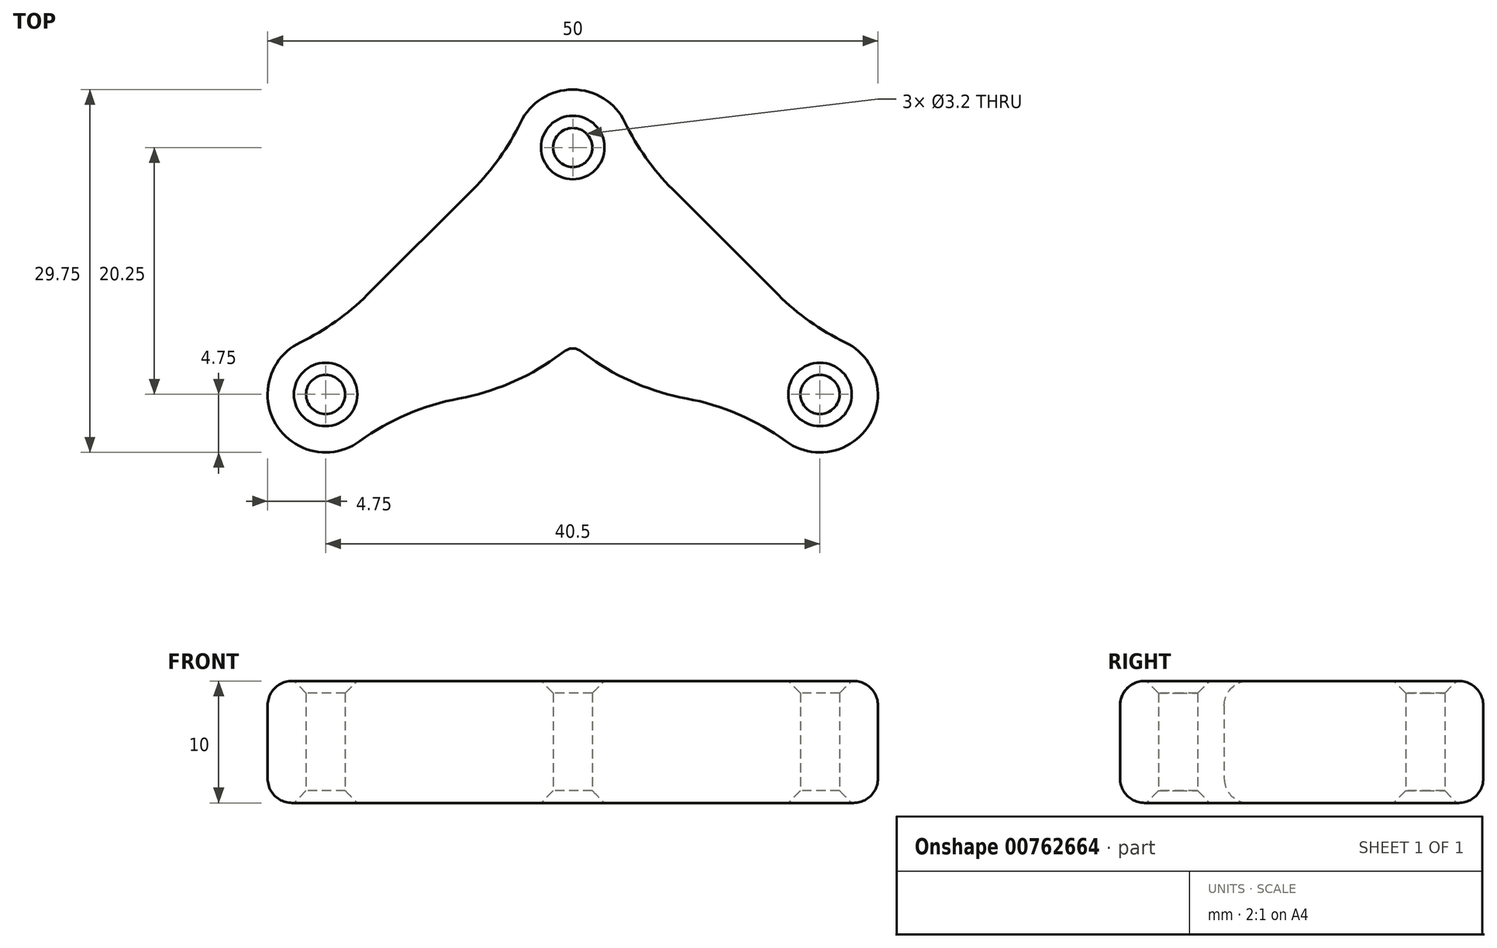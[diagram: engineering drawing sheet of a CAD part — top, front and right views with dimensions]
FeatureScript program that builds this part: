
annotation { "Feature Type Name" : "Feature", "Feature Type Description" : "" }
export const myFeature = defineFeature(function(context is Context, id is Id, definition is map)
    precondition{}
    {
        {
            var Q0;
            Q0=qCreatedBy(makeId("Top.planeOp"),FACE);
            var sketch = newSketch(context, id + "F0", { "sketchPlane" : qUnion([Q0])});
            skLineSegment(sketch, "E0", {"start": v(16.84, 8.16) * mm, "end": v(8.16, 16.84) * mm});
            skLineSegment(sketch, "E1", {"start": v(0, 3.78) * mm, "end": v(0, 4) * mm});
            skArc(sketch, "E2", {"start": v(0, 18.65) * mm, "mid": v(1.6, 20.25) * mm, "end": v(0, 21.85) * mm});
            skCircle(sketch, "E3", {"center": v(20.25, 0) * mm, "radius": 1.6 * mm});
            skArc(sketch, "E4", {"start": v(17.45, -3.84) * mm, "mid": v(24.33, -2.44) * mm, "end": v(22.3, 4.28) * mm});
            skArc(sketch, "E5", {"start": v(4.28, 22.3) * mm, "mid": v(2.53, 24.27) * mm, "end": v(0, 25) * mm});
            skPoint(sketch, "E6.visualSharp", {"position": v(4.75, 20.25) * mm});
            skArc(sketch, "E6.filletArc", {"start": v(4.28, 22.3) * mm, "mid": v(5.99, 19.41) * mm, "end": v(8.16, 16.84) * mm});
            skPoint(sketch, "E7.visualSharp", {"position": v(20.25, 4.75) * mm});
            skArc(sketch, "E7.filletArc", {"start": v(16.84, 8.16) * mm, "mid": v(19.41, 5.99) * mm, "end": v(22.3, 4.28) * mm});
            skArc(sketch, "E8.filletArc", {"start": v(17.45, -3.84) * mm, "mid": v(13.58, -1.63) * mm, "end": v(9.32, -0.34) * mm});
            skLineSegment(sketch, "E9", {"start": v(0, 4) * mm, "end": v(0, 3.78) * mm});
            skLineSegment(sketch, "E10", {"start": v(0.58, 3.6) * mm, "end": v(1.44, 2.99) * mm});
            skPoint(sketch, "E11.visualSharp", {"position": v(5.67, 0) * mm});
            skArc(sketch, "E11.filletArc", {"start": v(1.44, 2.99) * mm, "mid": v(5.2, 0.9) * mm, "end": v(9.32, -0.34) * mm});
            skArc(sketch, "E12.MirrorCS", {"start": v(-4.28, 22.3) * mm, "mid": v(-2.53, 24.27) * mm, "end": v(0, 25) * mm});
            skPoint(sketch, "E13.MirrorP", {"position": v(-4.75, 20.25) * mm});
            skArc(sketch, "E14.MirrorCS", {"start": v(-4.28, 22.3) * mm, "mid": v(-5.99, 19.41) * mm, "end": v(-8.16, 16.84) * mm});
            skLineSegment(sketch, "E15.MirrorCS", {"start": v(-16.84, 8.16) * mm, "end": v(-8.16, 16.84) * mm});
            skArc(sketch, "E16.MirrorCS", {"start": v(-16.84, 8.16) * mm, "mid": v(-19.41, 5.99) * mm, "end": v(-22.3, 4.28) * mm});
            skArc(sketch, "E17.MirrorCS", {"start": v(-17.45, -3.84) * mm, "mid": v(-24.33, -2.44) * mm, "end": v(-22.3, 4.28) * mm});
            skArc(sketch, "E18.MirrorCS", {"start": v(-17.45, -3.84) * mm, "mid": v(-13.58, -1.63) * mm, "end": v(-9.32, -0.34) * mm});
            skArc(sketch, "E19.MirrorCS", {"start": v(-1.44, 2.99) * mm, "mid": v(-5.2, 0.9) * mm, "end": v(-9.32, -0.34) * mm});
            skCircle(sketch, "E20.MirrorC", {"center": v(-20.25, 0) * mm, "radius": 1.6 * mm});
            skArc(sketch, "E21.MirrorCS", {"start": v(0, 18.65) * mm, "mid": v(-1.6, 20.25) * mm, "end": v(0, 21.85) * mm});
            skLineSegment(sketch, "E22.MirrorCS", {"start": v(-0.58, 3.6) * mm, "end": v(-1.44, 2.99) * mm});
            skPoint(sketch, "E23.visualSharp", {"position": v(0, 4) * mm});
            skArc(sketch, "E23.filletArc", {"start": v(0.58, 3.6) * mm, "mid": v(0, 3.78) * mm, "end": v(-0.58, 3.6) * mm});
            skPoint(sketch, "E24.orphan", {"position": v(0, 0) * mm});
            skSolve(sketch);
        }
        {
            var Q0;
            Q0 = qSketchRegion(id + "F0", true);
            extrude(context, id + "F1", {"entities" : qUnion([Q0]), "depth" : 10 * mm, "offsetDistance" : 25 * mm});
        }
        {
            var Q0;
            Q0=makeQuery(id+"F1.opExtrude","CAP_EDGE",EDGE,{"disambiguationData":[OSD([sQuery(id+"F0.wireOp",EDGE,"E19.MirrorCS")])],"isStart":false});
            var Q1;
            Q1=makeQuery(id+"F1.opExtrude","CAP_EDGE",EDGE,{"disambiguationData":[OSD([sQuery(id+"F0.wireOp",EDGE,"E19.MirrorCS")])],"isStart":true});
            var Q2;
            Q2=makeQuery(id+"F1.opExtrude","CAP_EDGE",EDGE,{"disambiguationData":[OSD([sQuery(id+"F0.wireOp",EDGE,"E15.MirrorCS")])],"isStart":false});
            var Q3;
            Q3=makeQuery(id+"F1.opExtrude","CAP_EDGE",EDGE,{"disambiguationData":[OSD([sQuery(id+"F0.wireOp",EDGE,"E16.MirrorCS")])],"isStart":false});
            fillet(context, id + "F2", {"entities" : qUnion([Q0, Q1, Q2, Q3]), "radius" : 2 * mm, "tangentPropagation" : true, "allowEdgeOverflow" : false});
        }
        {
            var Q0;
            Q0=makeQuery(id+"F1.opExtrude","CAP_EDGE",EDGE,{"disambiguationData":[OSD([sQuery(id+"F0.wireOp",EDGE,"E2"),sQuery(id+"F0.wireOp",EDGE,"E21.MirrorCS")])],"isStart":false});
            var Q1;
            Q1=makeQuery(id+"F1.opExtrude","CAP_EDGE",EDGE,{"disambiguationData":[OSD([sQuery(id+"F0.wireOp",EDGE,"E20.MirrorC")])],"isStart":false});
            var Q2;
            Q2=makeQuery(id+"F1.opExtrude","CAP_EDGE",EDGE,{"disambiguationData":[OSD([sQuery(id+"F0.wireOp",EDGE,"E3")])],"isStart":false});
            var Q3;
            Q3=makeQuery(id+"F1.opExtrude","CAP_EDGE",EDGE,{"disambiguationData":[OSD([sQuery(id+"F0.wireOp",EDGE,"E20.MirrorC")])],"isStart":true});
            var Q4;
            Q4=makeQuery(id+"F1.opExtrude","CAP_EDGE",EDGE,{"disambiguationData":[OSD([sQuery(id+"F0.wireOp",EDGE,"E2"),sQuery(id+"F0.wireOp",EDGE,"E21.MirrorCS")])],"isStart":true});
            var Q5;
            Q5=makeQuery(id+"F1.opExtrude","CAP_EDGE",EDGE,{"disambiguationData":[OSD([sQuery(id+"F0.wireOp",EDGE,"E3")])],"isStart":true});
            chamfer(context, id + "F3", {"entities" : qUnion([Q0, Q1, Q2, Q3, Q4, Q5]), "width" : 1 * mm, "tangentPropagation" : true});
        }
    });
